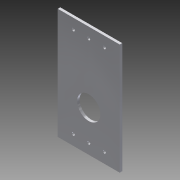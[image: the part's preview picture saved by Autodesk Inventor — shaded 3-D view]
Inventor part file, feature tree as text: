
AUTODESK INVENTOR PART (.ipt)
format: ipt  version: 2015 (Build 190159000, 159)  size: 135,168 bytes
history: native  units: in
note: dims shown in document units (in); Inventor stores cm internally (conversion verified against a paired STEP export)
features: other x4, hole x2
ambient origin geometry x8: Origin, YZ Plane, XZ Plane, XY Plane, X Axis, Y Axis, Z Axis, Center Point
bodies: Solid1 (feature_tree)
feature tree (6):
  hole  "rivet_holes"  [1 undecoded]
  hole  "bearing_hole"  [1 undecoded]
  other  "face_sketch"
  other  "Plate1"
  other  "rivet_holes_sketch"
  other  "bearing_hole_sketch"
note: 2 required parameter values undecoded (feature->parameter linkage not recoverable at this tier; creation-order binding heuristic only, values carry confidence <= 0.55)
